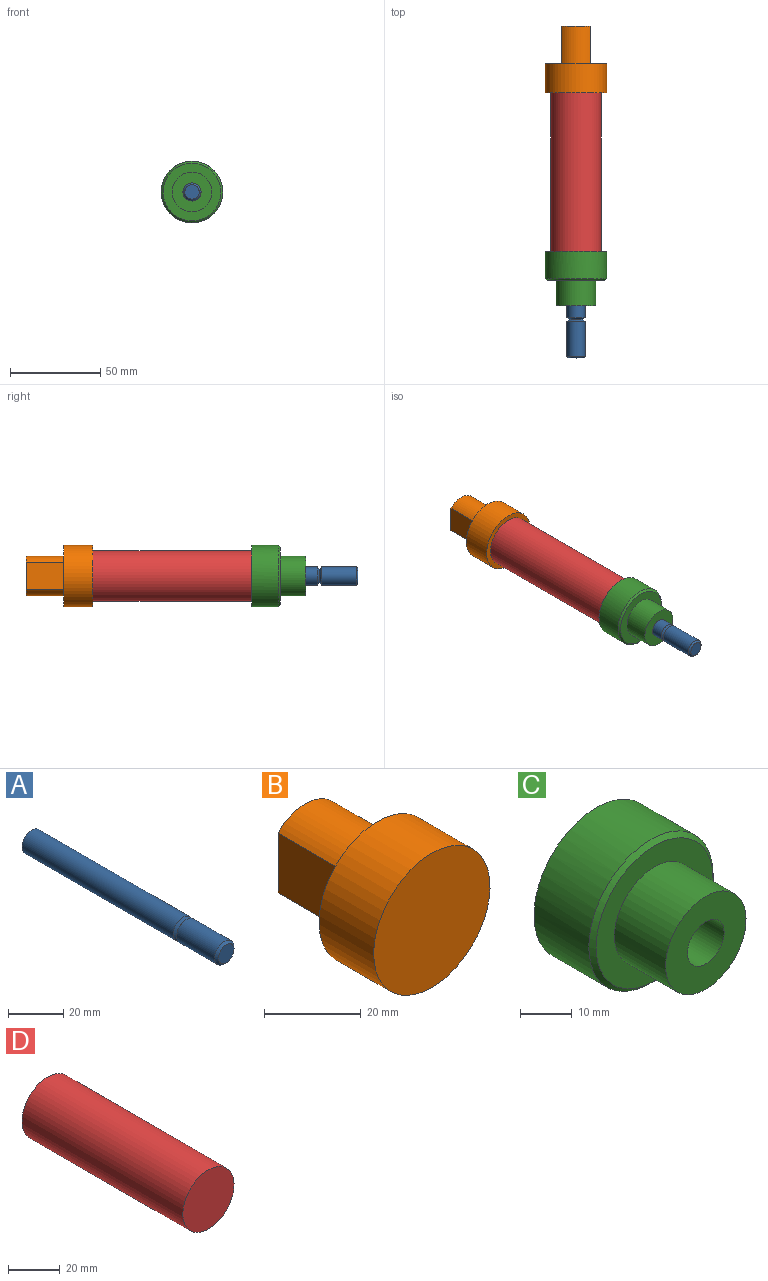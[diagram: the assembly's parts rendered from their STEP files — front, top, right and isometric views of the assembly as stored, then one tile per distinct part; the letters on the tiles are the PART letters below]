
ASSEMBLY  parts=4 mates=3
PART A: 7 faces, bbox 10x100x10 mm
  f0: cylinder r=5mm len=19.47mm, axis (0,-1,0), area 611.6mm2, adj f2,f6
  f1: plane 8x8mm, normal (0,-1,0), area 50.3mm2, adj f6
  f2: cone r=8.3mm half-angle=54.7deg, axis (0,-1,0), area 44.4mm2, adj f0,f3
  f3: cone r=3.67mm half-angle=55.7deg, axis (0,1,0), area 43.9mm2, adj f2,f5
  f4: plane 10x10mm, normal (0,1,0), area 78.5mm2, adj f5
  f5: cylinder r=5mm len=77.69mm, axis (0,-1,0), area 2440.5mm2, adj f3,f4
  f6: cone r=4mm half-angle=45deg, axis (0,1,0), area 40mm2, adj f0,f1
PART B: 8 faces, bbox 34x37x34 mm
  f0: plane 22x16mm, normal (0,1,0), area 317.9mm2, adj f1,f2,f6,f7
  f1: cylinder r=11mm len=21mm, axis (0,1,0), area 376.2mm2, adj f0,f4,f6,f7
  f2: cylinder r=11mm len=21mm, axis (0,1,0), area 376.2mm2, adj f0,f4,f6,f7
  f3: plane 34x34mm, normal (0,-1,0), area 907.9mm2, adj f5
  f4: plane 34x34mm, normal (0,1,0), area 590.1mm2, adj f1,f2,f5,f6,f7
  f5: cylinder r=17mm len=34mm, axis (0,1,0), area 1709mm2, adj f3,f4
  f6: plane 21x15.1mm, normal (1,0,0), area 317.1mm2, adj f0,f1,f2,f4
  f7: plane 21x15.1mm, normal (-1,0,0), area 317.1mm2, adj f0,f1,f2,f4
PART C: 7 faces, bbox 34x30x34 mm
  f0: plane 34x34mm, normal (0,1,0), area 829.4mm2, adj f1,f5
  f1: cylinder r=17mm len=34mm, axis (0,-1,0), area 1602.2mm2, adj f0,f6
  f2: plane 32x32mm, normal (0,-1,0), area 424.1mm2, adj f3,f6
  f3: cylinder r=11mm len=22mm, axis (0,-1,0), area 967.6mm2, adj f2,f4
  f4: plane 22x22mm, normal (0,-1,0), area 301.6mm2, adj f3,f5
  f5: cylinder r=5mm len=30mm, axis (0,-1,0), area 942.5mm2, adj f0,f4
  f6: cone r=16mm half-angle=45deg, axis (0,1,0), area 146.6mm2, adj f1,f2
PART D: 3 faces, bbox 28x88x28 mm
  f0: plane 28x28mm, normal (0,1,0), area 615.8mm2, adj f1
  f1: cylinder r=14mm len=88mm, axis (0,-1,0), area 7740.9mm2, adj f0,f2
  f2: plane 28x28mm, normal (0,-1,0), area 615.8mm2, adj f1
PLACE A t=(0,-59,0)mm
PLACE B t=(0,-60,0)mm
PLACE C t=(0,-60,0)mm
PLACE D t=(0,-60,0)mm
MATE fastened C.f1 <-> D.f1  axis (0,1,0) through (0,-44,0)mm
MATE fastened B.f1 <-> D.f1  axis (0,-1,0) through (0,44,0)mm
MATE slider A.f0 <-> C.f1  axis (0,-1,0) through (0,-102,0)mm
